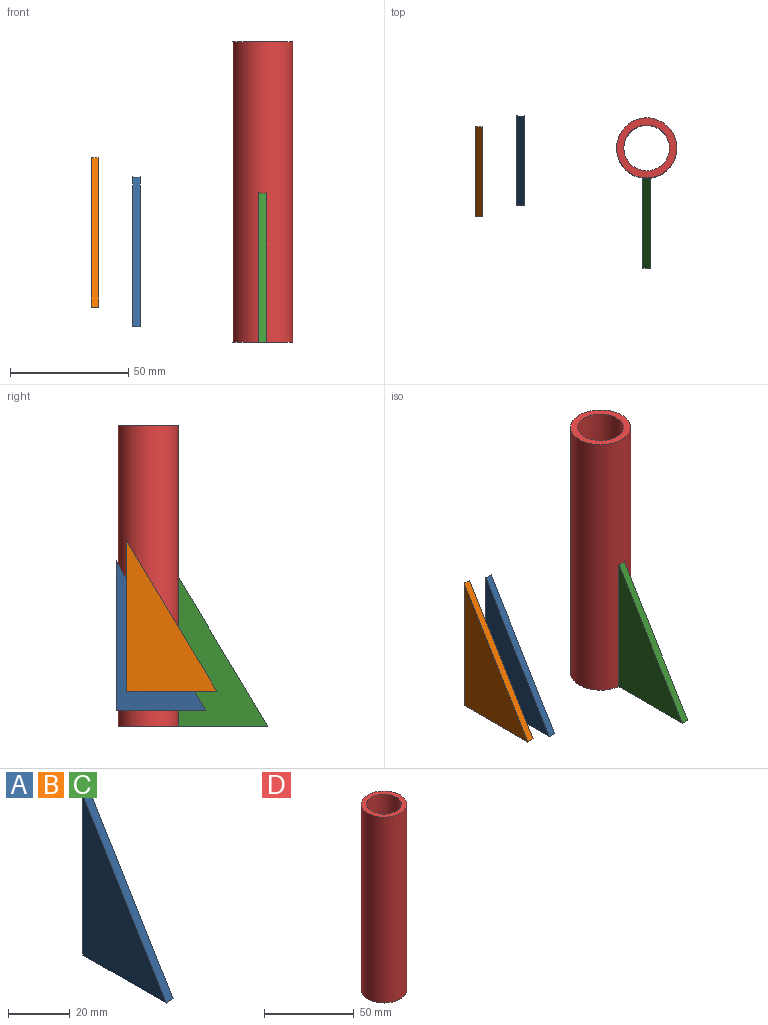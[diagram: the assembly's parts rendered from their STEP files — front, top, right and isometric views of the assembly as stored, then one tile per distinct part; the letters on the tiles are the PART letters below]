
ASSEMBLY  parts=4 mates=1
PART A: 5 faces, bbox 3.2x37.9x63.2 mm
  f0: plane 37.95x3.18mm, normal (0,0,-1), area 120.3mm2, adj f1,f2,f3,f4
  f1: plane 63.24x37.95mm, normal (-1,0,0), area 1199.9mm2, adj f0,f3,f4
  f2: plane 63.24x37.95mm, normal (1,0,0), area 1199.9mm2, adj f0,f3,f4
  f3: plane 63.24x37.95mm, normal (0,-0.86,0.51), area 233.8mm2, adj f0,f1,f2,f4
  f4: cylinder r=12.7mm len=63.24mm, axis (0,0,-1), area 201mm2, adj f0,f1,f2,f3
PART B: same geometry as A
PART C: same geometry as A
PART D: 4 faces, bbox 25.4x25.4x127 mm
  f0: cylinder r=9.65mm len=127mm, axis (0,0,-1), area 7702mm2, adj f2,f3
  f1: cylinder r=12.7mm len=127mm, axis (0,0,-1), area 10134.1mm2, adj f2,f3
  f2: plane 25.4x25.4mm, normal (0,0,1), area 214mm2, adj f0,f1
  f3: plane 25.4x25.4mm, normal (0,0,-1), area 214mm2, adj f0,f1
PLACE A t=(-53.32,13.79,6.55)mm
PLACE B t=(-70.81,9.22,14.84)mm
PLACE C t=(0,-12.45,-0.12)mm
PLACE D at identity
MATE fastened C.f4 <-> D.f1  axis (0,0,-1) through (0,0,63.5)mm
